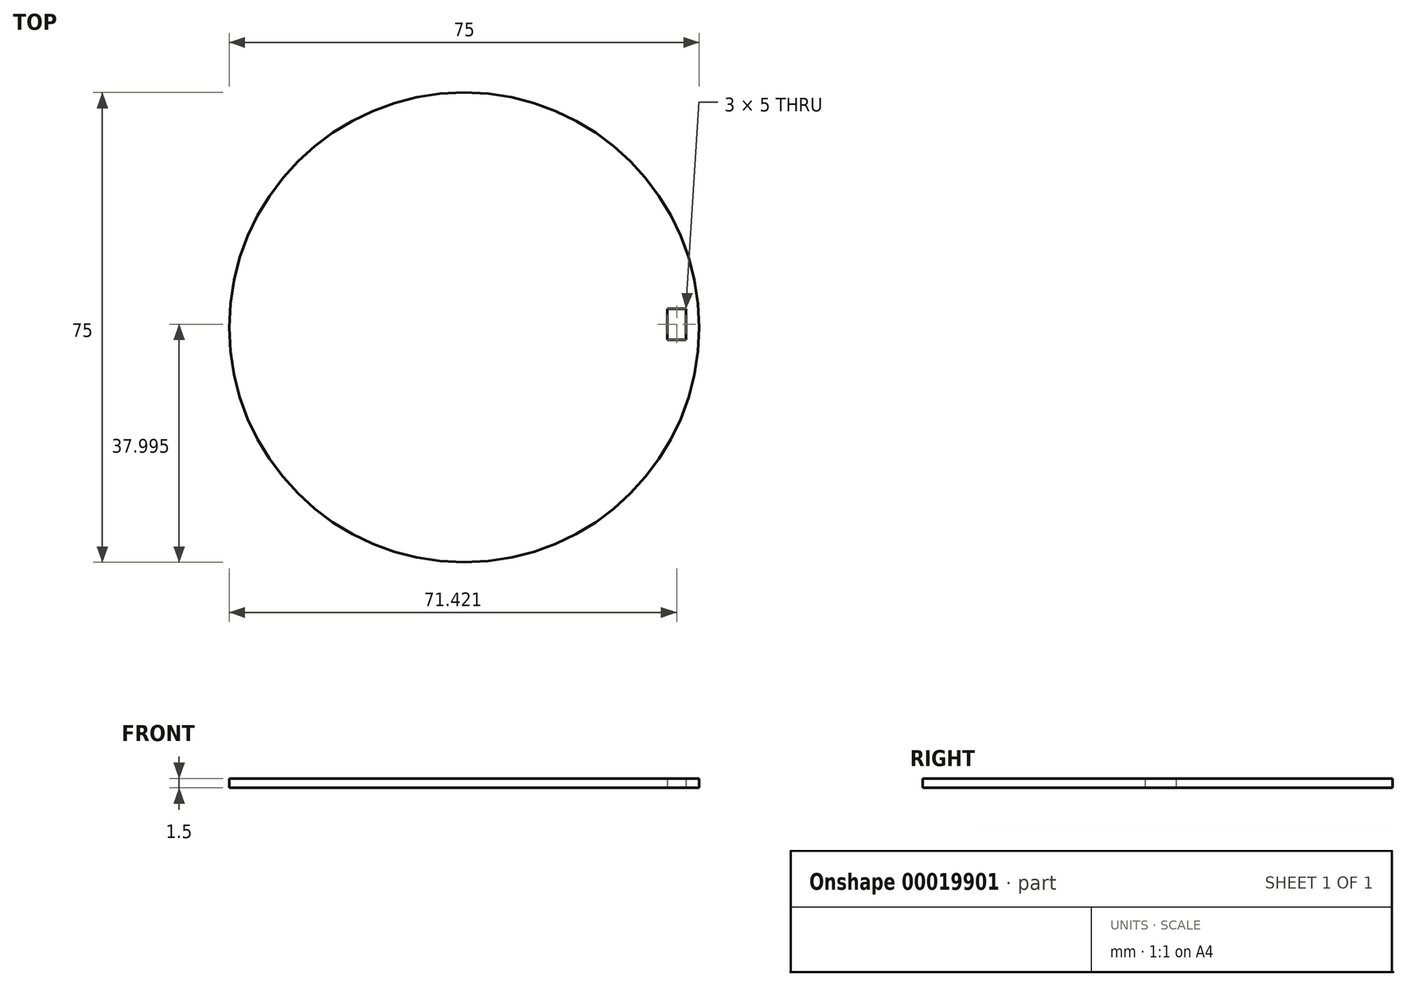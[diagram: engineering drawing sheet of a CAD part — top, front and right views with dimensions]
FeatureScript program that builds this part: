
annotation { "Feature Type Name" : "Feature", "Feature Type Description" : "" }
export const myFeature = defineFeature(function(context is Context, id is Id, definition is map)
    precondition{}
    {
        {
            var Q0;
            Q0=qCreatedBy(makeId("Top.planeOp"),FACE);
            var sketch = newSketch(context, id + "F0", { "sketchPlane" : qUnion([Q0])});
            skCircle(sketch, "E0", {"center": v(0, 0) * mm, "radius": 37.5 * mm});
            skLineSegment(sketch, "E1", {"start": v(32.42, -2) * mm, "end": v(32.42, 3) * mm});
            skLineSegment(sketch, "E2", {"start": v(32.42, 3) * mm, "end": v(35.42, 3) * mm});
            skLineSegment(sketch, "E3", {"start": v(35.42, 3) * mm, "end": v(35.42, -2) * mm});
            skLineSegment(sketch, "E4", {"start": v(32.42, -2) * mm, "end": v(35.42, -2) * mm});
            skSolve(sketch);
        }
        {
            var Q0;
            Q0=makeQuery(id+"F0.imprint","IMPRINT",FACE,{"disambiguationData":[TD([[makeQuery(id+"F0.imprint","IMPRINT",EDGE,{"derivedFrom":sQuery(id+"F0.wireOp",EDGE,"ugDZwq8R-vzUT-KqB2-XpK0-QCQeNDZ2EBAn")}),1.0]])]});
            var Q1;
            Q1=makeQuery(id+"F0.imprint","IMPRINT",FACE,{"disambiguationData":[TD([[makeQuery(id+"F0.imprint","IMPRINT",EDGE,{"derivedFrom":sQuery(id+"F0.wireOp",EDGE,"E0")}),1.0]])]});
            extrude(context, id + "F1", {"entities" : qUnion([Q0, Q1]), "depth" : 1.5 * mm});
        }
    });
